# Revit family: Lighting_Desk-Table_Nordlux_Shapes-Table
name_source: partatom
category: Lighting Fixtures
revit_build: Autodesk Revit 2018 (Build: 20190510_1515(x64)
units: mm (PartAtom-declared; Revit-internal decimal feet)

## family parameters
Always vertical = No
Cut with Voids When Loaded = No
Light Source = Yes
OmniClass Number = 23.35.47.11
OmniClass Title = Lighting Fixtures
Part Type = Normal
Room Calculation Point = No
Round Connector Dimension = Use Diameter
Shared = No
Work Plane-Based = Yes

## types (1)
- ART - (2120055035)
    Apparent Load = 6 VA
    BIMobject category = Desk & Table
    Beam angle = 286.00°
    Body material = Nordlux  - Metal  - Brass
    CQS = 81.7
    CRI / Ra = 81.7
    Color Filter = 16777215
    Default Elevation = 1219 mm
    Description = The Shapes series by Danish designer Maria Berntsen draws inspiration from elegant, organically shaped jewellery. The opal glass shade is carried out in a unique, asymmetrical form that plays beautifully together with the shiny brass base and creates a refined and intriguing expression. The lamp emits a soft and diffused light trough the mouth blown glass shade.
    Design country = Denmark
    Dimming Lamp Color Temperature Shift = <None>
    EANNumber = 2120055035
    Edition number = 1
    Flicker frequency = 102 Hz
    IFC Classification = Light Fixture
    Installation instructions = https://asset.productmarketingcloud.com
    Manufacturer = Nordlux
    Manufacturer country = China
    Manufacturer name = Nordlux
    Material main = Metal
    Material secondary = Glass
    Model = Shapes Table
    NominalVoltage = 230 V
    OmniClass Code = 23-35 47 11
    OmniClass Description = Lighting Fixtures
    Peak [cd] = 65.9
    Photometric Web File = Shapes 22.ies
    Power factor = 0.56
    Product Guid = 687f3695-6f86-4e8e-91b5-dd7a7d78582d
    Product SKU = Shapes-Table
    Product data url = https://bimobject.com
    Product family = Lighting
    Product group = Table
    Product name = Shapes Table
    Product url = https://nordlux.com
    QR code = https://bimobject.com
    Shade material = Nordlux  - Glass  - Milky glass
    TM30 Rf = 83.9
    TM30 Rg = 92.5
    Tilt Angle = 0.00°
    URL = www.nordlux.com
    Weight Net (Kg) = 1,8
    Youtube clip = https://www.youtube.com

## geometry (parser evidence)
native form markers: Sweep x4
no freeform markers — native parametric forms only
